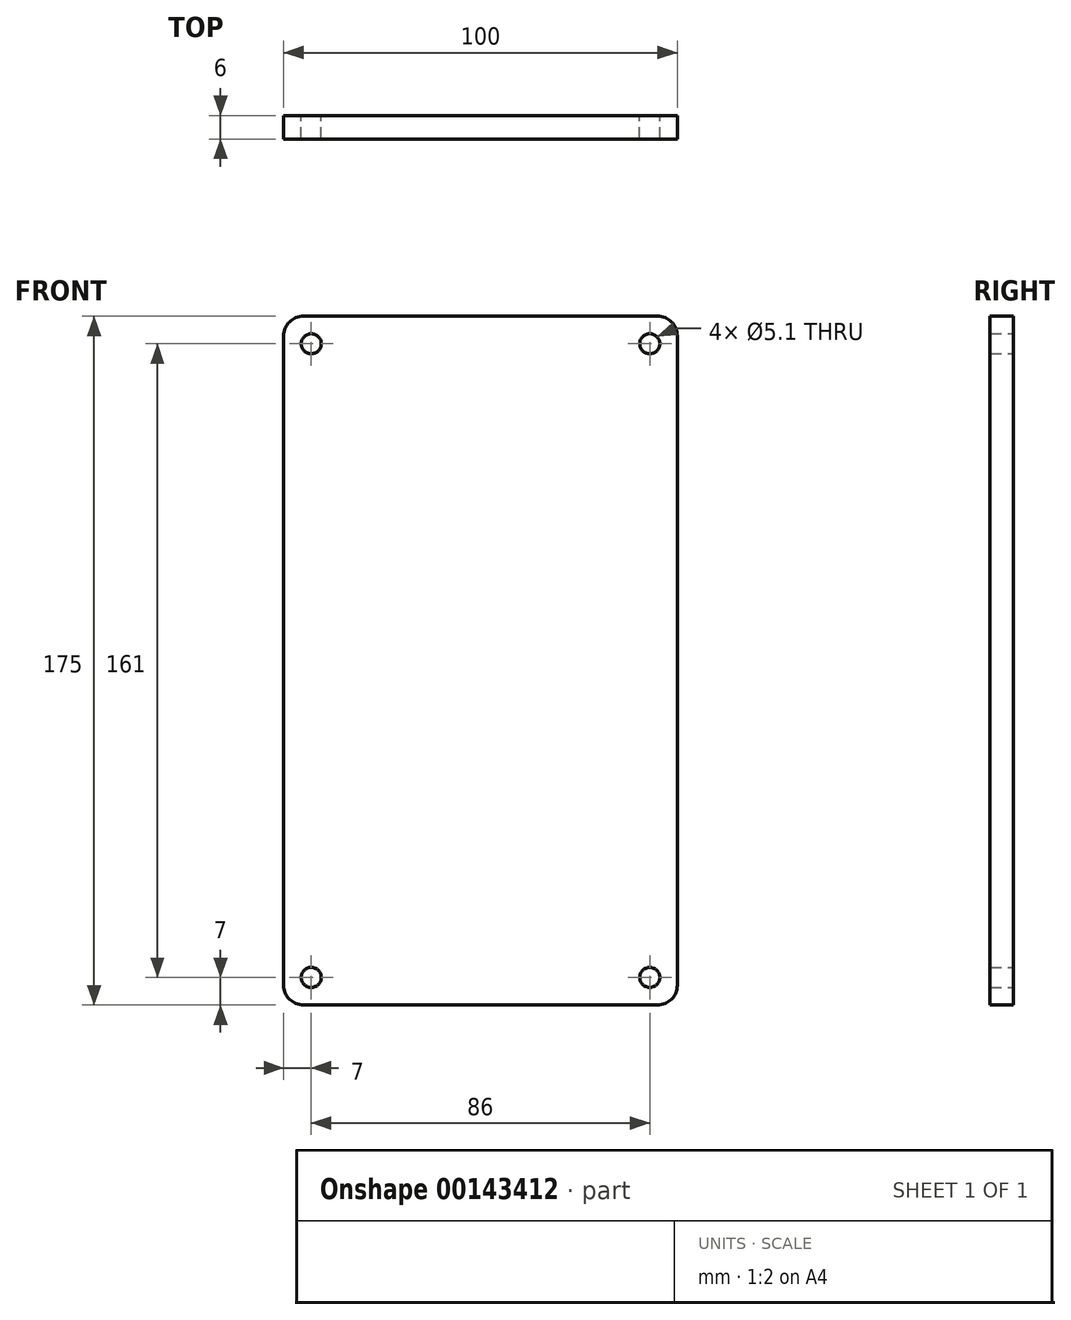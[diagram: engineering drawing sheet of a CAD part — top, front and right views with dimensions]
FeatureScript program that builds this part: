
annotation { "Feature Type Name" : "Feature", "Feature Type Description" : "" }
export const myFeature = defineFeature(function(context is Context, id is Id, definition is map)
    precondition{}
    {
        {
            var Q0;
            Q0=qCreatedBy(makeId("Front.planeOp"),FACE);
            var sketch = newSketch(context, id + "F0", { "sketchPlane" : qUnion([Q0])});
            skLineSegment(sketch, "E0.bottom", {"start": v(50, 87.5) * mm, "end": v(-50, 87.5) * mm});
            skLineSegment(sketch, "E0.top", {"start": v(50, -87.5) * mm, "end": v(-50, -87.5) * mm});
            skLineSegment(sketch, "E0.left", {"start": v(50, 87.5) * mm, "end": v(50, -87.5) * mm});
            skLineSegment(sketch, "E0.right", {"start": v(-50, 87.5) * mm, "end": v(-50, -87.5) * mm});
            skPoint(sketch, "E0.middle", {"position": v(0, 0) * mm});
            skLineSegment(sketch, "E1.bottom", {"start": v(-43, 80.5) * mm, "end": v(43, 80.5) * mm, "construction": true});
            skLineSegment(sketch, "E1.top", {"start": v(-43, -80.5) * mm, "end": v(43, -80.5) * mm, "construction": true});
            skLineSegment(sketch, "E1.left", {"start": v(-43, 80.5) * mm, "end": v(-43, -80.5) * mm, "construction": true});
            skLineSegment(sketch, "E1.right", {"start": v(43, 80.5) * mm, "end": v(43, -80.5) * mm, "construction": true});
            skCircle(sketch, "E2", {"center": v(-43, 80.5) * mm, "radius": 2.55 * mm});
            skCircle(sketch, "E3", {"center": v(43, 80.5) * mm, "radius": 2.55 * mm});
            skCircle(sketch, "E4", {"center": v(43, -80.5) * mm, "radius": 2.55 * mm});
            skCircle(sketch, "E5", {"center": v(-43, -80.5) * mm, "radius": 2.55 * mm});
            skSolve(sketch);
        }
        {
            var Q0;
            Q0=makeQuery(id+"F0.imprint","IMPRINT",FACE,{"disambiguationData":[TD([[makeQuery(id+"F0.imprint","IMPRINT",EDGE,{"derivedFrom":sQuery(id+"F0.wireOp",EDGE,"E0.bottom")}),1.0]])]});
            extrude(context, id + "F1", {"entities" : qUnion([Q0]), "depth" : 6 * mm});
        }
        {
            var Q0;
            Q0=makeQuery(id+"F1.opExtrude","SWEPT_EDGE",EDGE,{"disambiguationData":[OSD([sQuery(id+"F0.wireOp",EDGE,"E0.bottom"),sQuery(id+"F0.wireOp",EDGE,"E0.right")])]});
            var Q1;
            Q1=makeQuery(id+"F1.opExtrude","SWEPT_EDGE",EDGE,{"disambiguationData":[OSD([sQuery(id+"F0.wireOp",EDGE,"E0.top"),sQuery(id+"F0.wireOp",EDGE,"E0.right")])]});
            var Q2;
            Q2=makeQuery(id+"F1.opExtrude","SWEPT_EDGE",EDGE,{"disambiguationData":[OSD([sQuery(id+"F0.wireOp",EDGE,"E0.bottom"),sQuery(id+"F0.wireOp",EDGE,"E0.left")])]});
            var Q3;
            Q3=makeQuery(id+"F1.opExtrude","SWEPT_EDGE",EDGE,{"disambiguationData":[OSD([sQuery(id+"F0.wireOp",EDGE,"E0.top"),sQuery(id+"F0.wireOp",EDGE,"E0.left")])]});
            fillet(context, id + "F2", {"entities" : qUnion([Q0, Q1, Q2, Q3]), "radius" : 5 * mm, "tangentPropagation" : true, "allowEdgeOverflow" : false});
        }
    });
